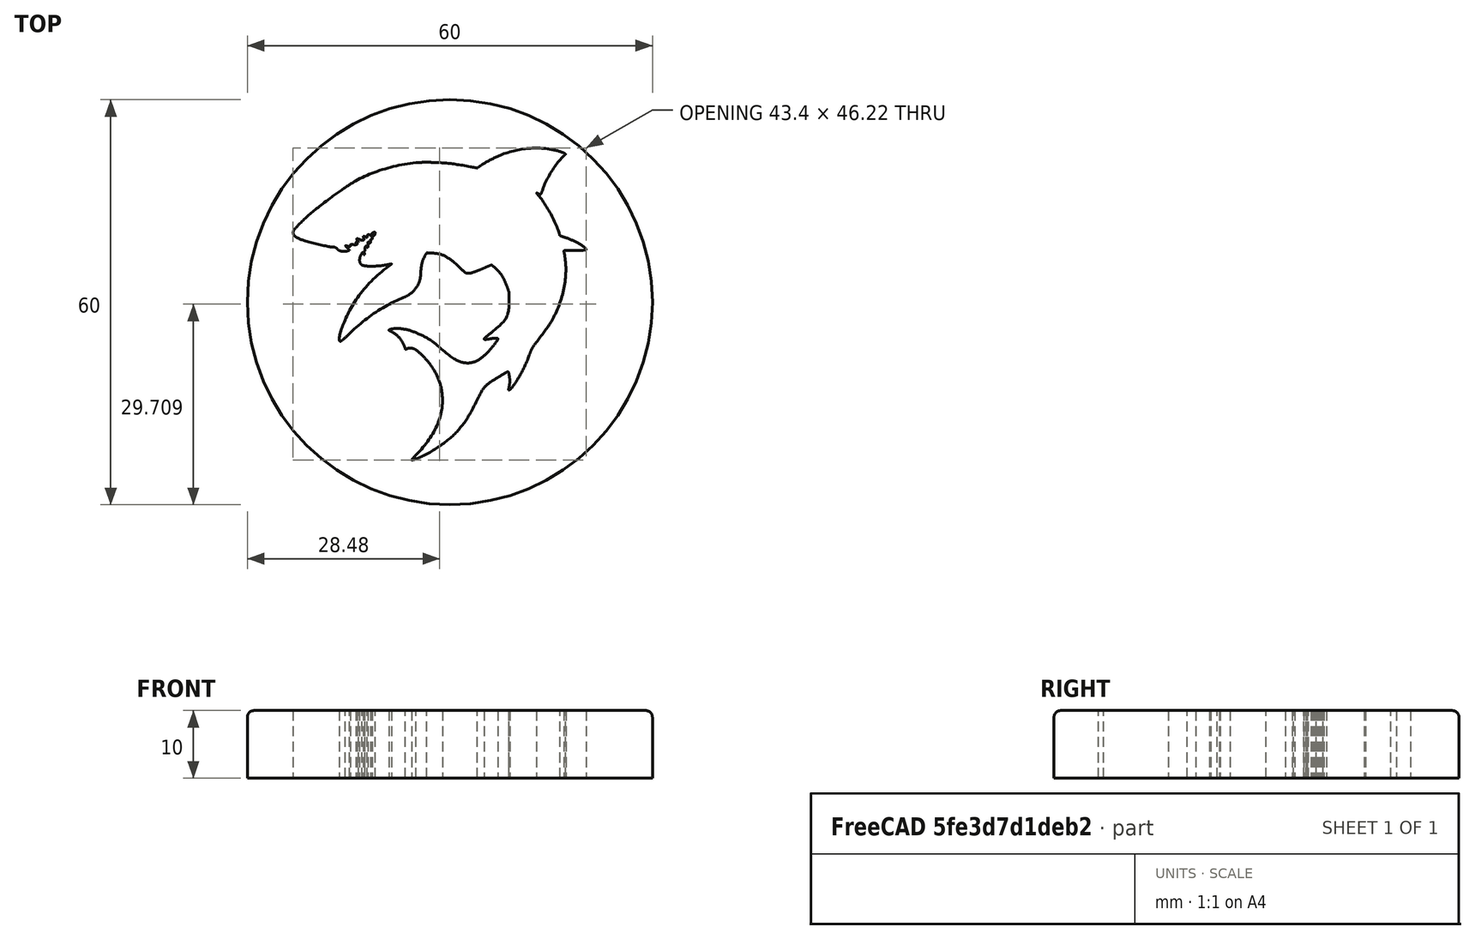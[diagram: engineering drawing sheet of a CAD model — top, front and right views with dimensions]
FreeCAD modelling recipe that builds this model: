
FCSTD DOCUMENT  (FreeCAD 0.18.4R)
Label: modeneda Tiburo
License: All rights reserved
LicenseURL: http://en.wikipedia.org/wiki/All_rights_reserved
objects: Sketcher::SketchObject×1, Part::Extrusion×1, Part::Cylinder×1, Part::Cut×1, Part::Fillet×1
note: 5 computed .brp shape members not serialized (recipe doc carries the construction recipe); baked Part::Feature solids carry a one-line shape summary decoded from their .brp

FEATURE [Sketcher::SketchObject] Sketch
  sketch-geometry (116):
    g0: BSplineCurve PolesCount=4 KnotsCount=2 Degree=3 IsPeriodic=0
    g1: BSplineCurve PolesCount=4 KnotsCount=2 Degree=3 IsPeriodic=0
    g2: BSplineCurve PolesCount=4 KnotsCount=2 Degree=3 IsPeriodic=0
    g3: BSplineCurve PolesCount=4 KnotsCount=2 Degree=3 IsPeriodic=0
    g4: BSplineCurve PolesCount=4 KnotsCount=2 Degree=3 IsPeriodic=0
    g5: BSplineCurve PolesCount=4 KnotsCount=2 Degree=3 IsPeriodic=0
    g6: BSplineCurve PolesCount=4 KnotsCount=2 Degree=3 IsPeriodic=0
    g7: BSplineCurve PolesCount=4 KnotsCount=2 Degree=3 IsPeriodic=0
    g8: BSplineCurve PolesCount=4 KnotsCount=2 Degree=3 IsPeriodic=0
    g9: BSplineCurve PolesCount=4 KnotsCount=2 Degree=3 IsPeriodic=0
    g10: BSplineCurve PolesCount=4 KnotsCount=2 Degree=3 IsPeriodic=0
    g11: BSplineCurve PolesCount=4 KnotsCount=2 Degree=3 IsPeriodic=0
    g12: BSplineCurve PolesCount=4 KnotsCount=2 Degree=3 IsPeriodic=0
    g13: BSplineCurve PolesCount=4 KnotsCount=2 Degree=3 IsPeriodic=0
    g14: BSplineCurve PolesCount=4 KnotsCount=2 Degree=3 IsPeriodic=0
    g15: BSplineCurve PolesCount=4 KnotsCount=2 Degree=3 IsPeriodic=0
    g16: BSplineCurve PolesCount=4 KnotsCount=2 Degree=3 IsPeriodic=0
    g17: BSplineCurve PolesCount=4 KnotsCount=2 Degree=3 IsPeriodic=0
    g18: BSplineCurve PolesCount=4 KnotsCount=2 Degree=3 IsPeriodic=0
    g19: BSplineCurve PolesCount=2 KnotsCount=2 Degree=1 IsPeriodic=0
    g20: BSplineCurve PolesCount=2 KnotsCount=2 Degree=1 IsPeriodic=0
    g21: BSplineCurve PolesCount=4 KnotsCount=2 Degree=3 IsPeriodic=0
    g22: BSplineCurve PolesCount=4 KnotsCount=2 Degree=3 IsPeriodic=0
    g23: BSplineCurve PolesCount=4 KnotsCount=2 Degree=3 IsPeriodic=0
    g24: BSplineCurve PolesCount=4 KnotsCount=2 Degree=3 IsPeriodic=0
    g25: BSplineCurve PolesCount=4 KnotsCount=2 Degree=3 IsPeriodic=0
    g26: BSplineCurve PolesCount=4 KnotsCount=2 Degree=3 IsPeriodic=0
    g27: BSplineCurve PolesCount=4 KnotsCount=2 Degree=3 IsPeriodic=0
    g28: BSplineCurve PolesCount=2 KnotsCount=2 Degree=1 IsPeriodic=0
    g29: BSplineCurve PolesCount=2 KnotsCount=2 Degree=1 IsPeriodic=0
    g30: BSplineCurve PolesCount=4 KnotsCount=2 Degree=3 IsPeriodic=0
    g31: BSplineCurve PolesCount=4 KnotsCount=2 Degree=3 IsPeriodic=0
    g32: BSplineCurve PolesCount=4 KnotsCount=2 Degree=3 IsPeriodic=0
    g33: BSplineCurve PolesCount=4 KnotsCount=2 Degree=3 IsPeriodic=0
    g34: BSplineCurve PolesCount=4 KnotsCount=2 Degree=3 IsPeriodic=0
    g35: BSplineCurve PolesCount=4 KnotsCount=2 Degree=3 IsPeriodic=0
    g36: BSplineCurve PolesCount=4 KnotsCount=2 Degree=3 IsPeriodic=0
    g37: BSplineCurve PolesCount=4 KnotsCount=2 Degree=3 IsPeriodic=0
    g38: BSplineCurve PolesCount=4 KnotsCount=2 Degree=3 IsPeriodic=0
    g39: BSplineCurve PolesCount=4 KnotsCount=2 Degree=3 IsPeriodic=0
    g40: BSplineCurve PolesCount=4 KnotsCount=2 Degree=3 IsPeriodic=0
    g41: BSplineCurve PolesCount=4 KnotsCount=2 Degree=3 IsPeriodic=0
    g42: BSplineCurve PolesCount=4 KnotsCount=2 Degree=3 IsPeriodic=0
    g43: BSplineCurve PolesCount=4 KnotsCount=2 Degree=3 IsPeriodic=0
    g44: BSplineCurve PolesCount=4 KnotsCount=2 Degree=3 IsPeriodic=0
    g45: BSplineCurve PolesCount=4 KnotsCount=2 Degree=3 IsPeriodic=0
    g46: BSplineCurve PolesCount=4 KnotsCount=2 Degree=3 IsPeriodic=0
    g47: BSplineCurve PolesCount=4 KnotsCount=2 Degree=3 IsPeriodic=0
    g48: BSplineCurve PolesCount=4 KnotsCount=2 Degree=3 IsPeriodic=0
    g49: BSplineCurve PolesCount=4 KnotsCount=2 Degree=3 IsPeriodic=0
    g50: BSplineCurve PolesCount=4 KnotsCount=2 Degree=3 IsPeriodic=0
    g51: BSplineCurve PolesCount=4 KnotsCount=2 Degree=3 IsPeriodic=0
    g52: BSplineCurve PolesCount=4 KnotsCount=2 Degree=3 IsPeriodic=0
    g53: BSplineCurve PolesCount=4 KnotsCount=2 Degree=3 IsPeriodic=0
    g54: BSplineCurve PolesCount=4 KnotsCount=2 Degree=3 IsPeriodic=0
    g55: BSplineCurve PolesCount=4 KnotsCount=2 Degree=3 IsPeriodic=0
    g56: BSplineCurve PolesCount=4 KnotsCount=2 Degree=3 IsPeriodic=0
    g57: BSplineCurve PolesCount=4 KnotsCount=2 Degree=3 IsPeriodic=0
    g58: BSplineCurve PolesCount=4 KnotsCount=2 Degree=3 IsPeriodic=0
    g59: BSplineCurve PolesCount=4 KnotsCount=2 Degree=3 IsPeriodic=0
    g60: BSplineCurve PolesCount=4 KnotsCount=2 Degree=3 IsPeriodic=0
    g61: BSplineCurve PolesCount=4 KnotsCount=2 Degree=3 IsPeriodic=0
    g62: BSplineCurve PolesCount=4 KnotsCount=2 Degree=3 IsPeriodic=0
    g63: BSplineCurve PolesCount=4 KnotsCount=2 Degree=3 IsPeriodic=0
    g64: BSplineCurve PolesCount=2 KnotsCount=2 Degree=1 IsPeriodic=0
    g65: BSplineCurve PolesCount=2 KnotsCount=2 Degree=1 IsPeriodic=0
    g66: BSplineCurve PolesCount=4 KnotsCount=2 Degree=3 IsPeriodic=0
    g67: BSplineCurve PolesCount=4 KnotsCount=2 Degree=3 IsPeriodic=0
    g68: BSplineCurve PolesCount=4 KnotsCount=2 Degree=3 IsPeriodic=0
    g69: BSplineCurve PolesCount=4 KnotsCount=2 Degree=3 IsPeriodic=0
    g70: BSplineCurve PolesCount=4 KnotsCount=2 Degree=3 IsPeriodic=0
    g71: BSplineCurve PolesCount=4 KnotsCount=2 Degree=3 IsPeriodic=0
    g72: BSplineCurve PolesCount=2 KnotsCount=2 Degree=1 IsPeriodic=0
    g73: BSplineCurve PolesCount=2 KnotsCount=2 Degree=1 IsPeriodic=0
    g74: BSplineCurve PolesCount=4 KnotsCount=2 Degree=3 IsPeriodic=0
    g75: BSplineCurve PolesCount=4 KnotsCount=2 Degree=3 IsPeriodic=0
    g76: BSplineCurve PolesCount=4 KnotsCount=2 Degree=3 IsPeriodic=0
    g77: BSplineCurve PolesCount=4 KnotsCount=2 Degree=3 IsPeriodic=0
    g78: BSplineCurve PolesCount=4 KnotsCount=2 Degree=3 IsPeriodic=0
    g79: BSplineCurve PolesCount=4 KnotsCount=2 Degree=3 IsPeriodic=0
    g80: BSplineCurve PolesCount=4 KnotsCount=2 Degree=3 IsPeriodic=0
    g81: BSplineCurve PolesCount=4 KnotsCount=2 Degree=3 IsPeriodic=0
    g82: BSplineCurve PolesCount=4 KnotsCount=2 Degree=3 IsPeriodic=0
    g83: BSplineCurve PolesCount=4 KnotsCount=2 Degree=3 IsPeriodic=0
    g84: BSplineCurve PolesCount=2 KnotsCount=2 Degree=1 IsPeriodic=0
    g85: BSplineCurve PolesCount=2 KnotsCount=2 Degree=1 IsPeriodic=0
    g86: BSplineCurve PolesCount=4 KnotsCount=2 Degree=3 IsPeriodic=0
    g87: BSplineCurve PolesCount=4 KnotsCount=2 Degree=3 IsPeriodic=0
    g88: BSplineCurve PolesCount=4 KnotsCount=2 Degree=3 IsPeriodic=0
    g89: BSplineCurve PolesCount=4 KnotsCount=2 Degree=3 IsPeriodic=0
    g90: BSplineCurve PolesCount=4 KnotsCount=2 Degree=3 IsPeriodic=0
    g91: BSplineCurve PolesCount=4 KnotsCount=2 Degree=3 IsPeriodic=0
    g92: BSplineCurve PolesCount=4 KnotsCount=2 Degree=3 IsPeriodic=0
    g93: BSplineCurve PolesCount=4 KnotsCount=2 Degree=3 IsPeriodic=0
    g94: BSplineCurve PolesCount=2 KnotsCount=2 Degree=1 IsPeriodic=0
    g95: BSplineCurve PolesCount=2 KnotsCount=2 Degree=1 IsPeriodic=0
    g96: BSplineCurve PolesCount=4 KnotsCount=2 Degree=3 IsPeriodic=0
    g97: BSplineCurve PolesCount=4 KnotsCount=2 Degree=3 IsPeriodic=0
    g98: BSplineCurve PolesCount=4 KnotsCount=2 Degree=3 IsPeriodic=0
    g99: BSplineCurve PolesCount=4 KnotsCount=2 Degree=3 IsPeriodic=0
    g100: BSplineCurve PolesCount=4 KnotsCount=2 Degree=3 IsPeriodic=0
    g101: BSplineCurve PolesCount=4 KnotsCount=2 Degree=3 IsPeriodic=0
    g102: BSplineCurve PolesCount=4 KnotsCount=2 Degree=3 IsPeriodic=0
    g103: BSplineCurve PolesCount=4 KnotsCount=2 Degree=3 IsPeriodic=0
    g104: BSplineCurve PolesCount=4 KnotsCount=2 Degree=3 IsPeriodic=0
    g105: BSplineCurve PolesCount=4 KnotsCount=2 Degree=3 IsPeriodic=0
    g106: BSplineCurve PolesCount=4 KnotsCount=2 Degree=3 IsPeriodic=0
    g107: BSplineCurve PolesCount=4 KnotsCount=2 Degree=3 IsPeriodic=0
    g108: BSplineCurve PolesCount=4 KnotsCount=2 Degree=3 IsPeriodic=0
    g109: BSplineCurve PolesCount=4 KnotsCount=2 Degree=3 IsPeriodic=0
    g110: BSplineCurve PolesCount=4 KnotsCount=2 Degree=3 IsPeriodic=0
    g111: BSplineCurve PolesCount=4 KnotsCount=2 Degree=3 IsPeriodic=0
    g112: BSplineCurve PolesCount=4 KnotsCount=2 Degree=3 IsPeriodic=0
    g113: BSplineCurve PolesCount=4 KnotsCount=2 Degree=3 IsPeriodic=0
    g114: BSplineCurve PolesCount=4 KnotsCount=2 Degree=3 IsPeriodic=0
    g115: BSplineCurve PolesCount=2 KnotsCount=2 Degree=1 IsPeriodic=0
  constraints (116):
    c: Coincident(g0,g1)
    c: Coincident(g1,g2)
    c: Coincident(g2,g3)
    c: Coincident(g3,g4)
    c: Coincident(g4,g5)
    c: Coincident(g5,g6)
    c: Coincident(g6,g7)
    c: Coincident(g7,g8)
    c: Coincident(g8,g9)
    c: Coincident(g9,g10)
    c: Coincident(g10,g11)
    c: Coincident(g11,g12)
    c: Coincident(g12,g13)
    c: Coincident(g13,g14)
    c: Coincident(g14,g15)
    c: Coincident(g15,g16)
    c: Coincident(g16,g17)
    c: Coincident(g17,g18)
    c: Coincident(g18,g19)
    c: Coincident(g19,g20)
    c: Coincident(g20,g21)
    c: Coincident(g21,g22)
    c: Coincident(g22,g23)
    c: Coincident(g23,g24)
    c: Coincident(g24,g25)
    c: Coincident(g25,g26)
    c: Coincident(g26,g27)
    c: Coincident(g27,g28)
    c: Coincident(g28,g29)
    c: Coincident(g29,g30)
    c: Coincident(g30,g31)
    c: Coincident(g31,g32)
    c: Coincident(g32,g33)
    c: Coincident(g33,g34)
    c: Coincident(g34,g35)
    c: Coincident(g35,g36)
    c: Coincident(g36,g37)
    c: Coincident(g37,g38)
    c: Coincident(g38,g39)
    c: Coincident(g39,g40)
    c: Coincident(g40,g41)
    c: Coincident(g41,g42)
    c: Coincident(g42,g43)
    c: Coincident(g43,g44)
    c: Coincident(g44,g45)
    c: Coincident(g45,g46)
    c: Coincident(g46,g47)
    c: Coincident(g47,g48)
    c: Coincident(g48,g49)
    c: Coincident(g49,g50)
    c: Coincident(g50,g51)
    c: Coincident(g51,g52)
    c: Coincident(g52,g53)
    c: Coincident(g53,g54)
    c: Coincident(g54,g55)
    c: Coincident(g55,g56)
    c: Coincident(g56,g57)
    c: Coincident(g57,g58)
    c: Coincident(g58,g59)
    c: Coincident(g59,g60)
    c: Coincident(g60,g61)
    c: Coincident(g61,g62)
    c: Coincident(g62,g63)
    c: Coincident(g63,g64)
    c: Coincident(g64,g65)
    c: Coincident(g65,g66)
    c: Coincident(g66,g67)
    c: Coincident(g67,g68)
    c: Coincident(g68,g69)
    c: Coincident(g69,g70)
    c: Coincident(g70,g71)
    c: Coincident(g71,g72)
    c: Coincident(g72,g73)
    c: Coincident(g73,g74)
    c: Coincident(g74,g75)
    c: Coincident(g75,g76)
    c: Coincident(g76,g77)
    c: Coincident(g77,g78)
    c: Coincident(g78,g79)
    c: Coincident(g79,g80)
    c: Coincident(g80,g81)
    c: Coincident(g81,g82)
    c: Coincident(g82,g83)
    c: Coincident(g83,g84)
    c: Coincident(g84,g85)
    c: Coincident(g85,g86)
    c: Coincident(g86,g87)
    c: Coincident(g87,g88)
    c: Coincident(g88,g89)
    c: Coincident(g89,g90)
    c: Coincident(g90,g91)
    c: Coincident(g91,g92)
    c: Coincident(g92,g93)
    c: Coincident(g93,g94)
    c: Coincident(g94,g95)
    c: Coincident(g95,g96)
    c: Coincident(g96,g97)
    c: Coincident(g97,g98)
    c: Coincident(g98,g99)
    c: Coincident(g99,g100)
    c: Coincident(g100,g101)
    c: Coincident(g101,g102)
    c: Coincident(g102,g103)
    c: Coincident(g103,g104)
    c: Coincident(g104,g105)
    c: Coincident(g105,g106)
    c: Coincident(g106,g107)
    c: Coincident(g107,g108)
    c: Coincident(g108,g109)
    c: Coincident(g109,g110)
    c: Coincident(g110,g111)
    c: Coincident(g111,g112)
    c: Coincident(g112,g113)
    c: Coincident(g113,g114)
    c: Coincident(g114,g115)
    c: Coincident(g115,g0)
FEATURE [Part::Extrusion] Extrude
  Base = -> Sketch
  Dir = (0,0,1)
  DirMode = 2
  FaceMakerClass = Part::FaceMakerBullseye
  LengthFwd = 10
  LengthRev = 0
  Placement = pos=(-28,26,0) rot=(0,0,1;0rad)
  Solid = true
  Symmetric = false
FEATURE [Part::Cylinder] Cylinder  label="Cilindro"
  Angle = 360
  AttacherType = Attacher::AttachEngine3D
  Height = 10
  Radius = 30
FEATURE [Part::Cut] Cut
  Base = -> Cylinder
  Tool = -> Extrude
FEATURE [Part::Fillet] Fillet
  Base = -> Cut
  Edges = 1 edges r=1: [Edge1]
